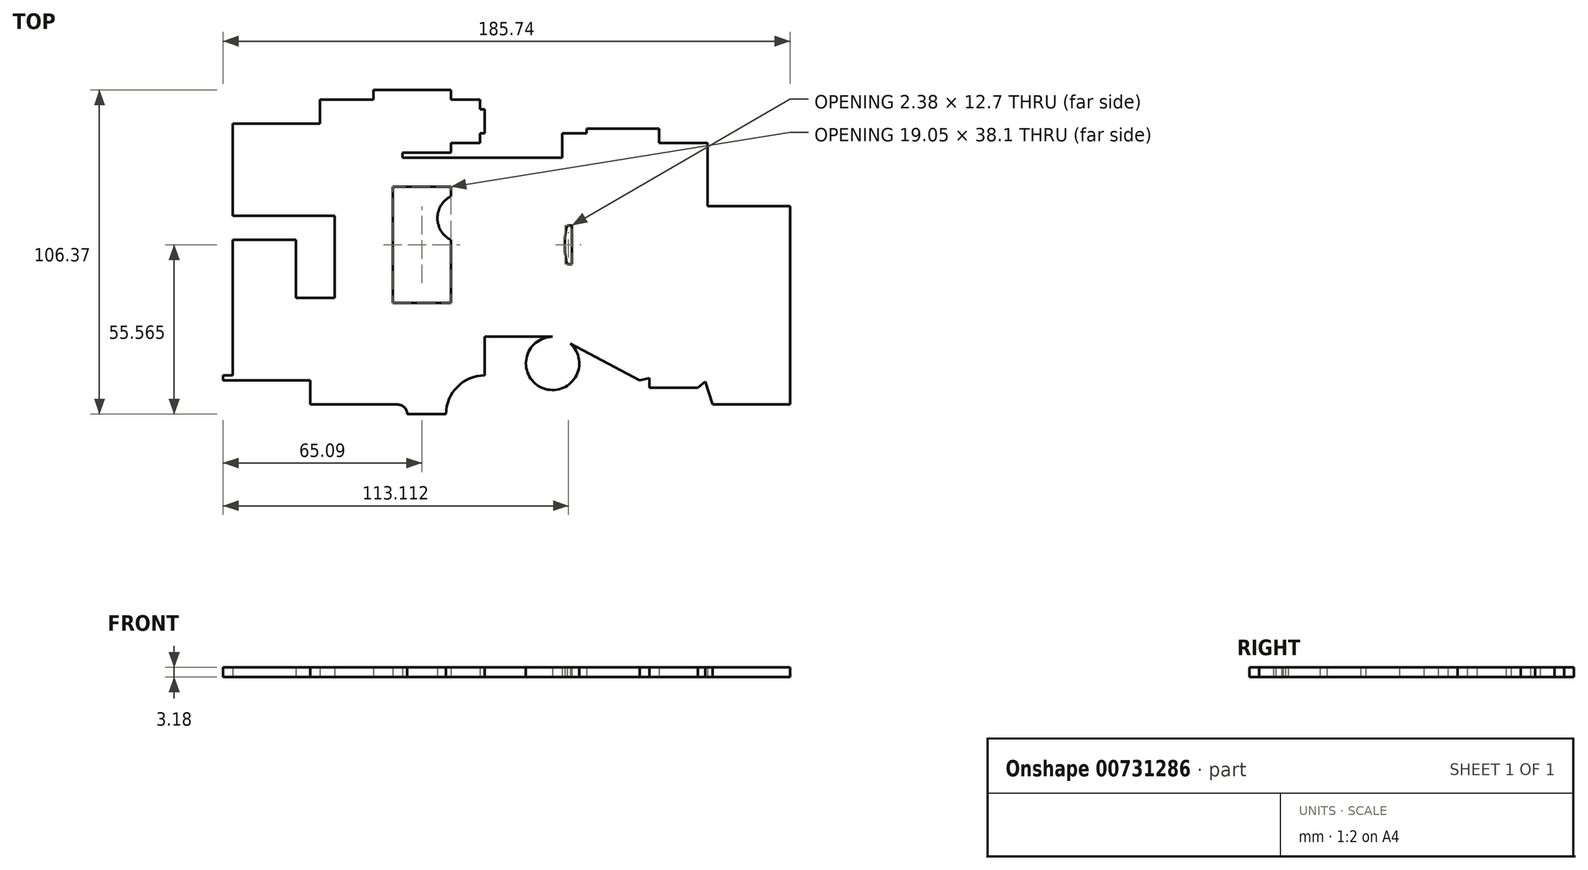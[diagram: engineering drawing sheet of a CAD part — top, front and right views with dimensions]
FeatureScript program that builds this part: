
annotation { "Feature Type Name" : "Feature", "Feature Type Description" : "" }
export const myFeature = defineFeature(function(context is Context, id is Id, definition is map)
    precondition{}
    {
        {
            var Q0;
            Q0=qCreatedBy(makeId("Top.planeOp"),FACE);
            var sketch = newSketch(context, id + "F0", { "sketchPlane" : qUnion([Q0])});
            skLineSegment(sketch, "E0.bottom", {"start": v(-55.56, 35.73) * mm, "end": v(-34.92, 35.73) * mm});
            skLineSegment(sketch, "E0.left", {"start": v(-55.56, 35.73) * mm, "end": v(-55.56, -8.72) * mm});
            skLineSegment(sketch, "E1", {"start": v(-55.56, -8.72) * mm, "end": v(-58.74, -8.72) * mm});
            skLineSegment(sketch, "E2", {"start": v(-58.74, -8.72) * mm, "end": v(-58.74, -10.3) * mm});
            skLineSegment(sketch, "E3", {"start": v(-58.74, -10.3) * mm, "end": v(-30.16, -10.3) * mm});
            skLineSegment(sketch, "E4", {"start": v(-30.16, -10.3) * mm, "end": v(-30.16, -18.24) * mm});
            skLineSegment(sketch, "E5", {"start": v(-30.16, -18.24) * mm, "end": v(-1.59, -18.24) * mm});
            skLineSegment(sketch, "E6", {"start": v(1.59, -21.42) * mm, "end": v(14.29, -21.42) * mm});
            skLineSegment(sketch, "E7", {"start": v(26.99, -8.72) * mm, "end": v(26.99, 3.98) * mm});
            skLineSegment(sketch, "E8", {"start": v(-34.92, 35.73) * mm, "end": v(-34.93, 16.68) * mm});
            skLineSegment(sketch, "E9", {"start": v(-34.92, 16.68) * mm, "end": v(-22.22, 16.68) * mm});
            skLineSegment(sketch, "E10", {"start": v(-22.22, 16.68) * mm, "end": v(-22.22, 43.67) * mm});
            skLineSegment(sketch, "E11", {"start": v(-22.22, 43.67) * mm, "end": v(-55.56, 43.67) * mm});
            skLineSegment(sketch, "E12", {"start": v(-55.56, 43.67) * mm, "end": v(-55.56, 73.83) * mm});
            skLineSegment(sketch, "E13", {"start": v(-55.56, 73.83) * mm, "end": v(-26.99, 73.83) * mm});
            skLineSegment(sketch, "E14", {"start": v(-26.99, 73.83) * mm, "end": v(-26.99, 81.77) * mm});
            skLineSegment(sketch, "E15", {"start": v(-26.99, 81.77) * mm, "end": v(-9.53, 81.77) * mm});
            skLineSegment(sketch, "E16", {"start": v(-9.53, 81.77) * mm, "end": v(-9.53, 84.95) * mm});
            skLineSegment(sketch, "E17", {"start": v(-9.53, 84.95) * mm, "end": v(15.87, 84.95) * mm});
            skLineSegment(sketch, "E18", {"start": v(15.87, 84.95) * mm, "end": v(15.87, 81.77) * mm});
            skLineSegment(sketch, "E19", {"start": v(15.87, 81.77) * mm, "end": v(25.4, 81.77) * mm});
            skLineSegment(sketch, "E20", {"start": v(25.4, 81.77) * mm, "end": v(25.4, 78.6) * mm});
            skLineSegment(sketch, "E21", {"start": v(25.4, 78.6) * mm, "end": v(26.99, 78.6) * mm});
            skLineSegment(sketch, "E22", {"start": v(26.99, 78.6) * mm, "end": v(26.99, 70.66) * mm});
            skLineSegment(sketch, "E23", {"start": v(26.99, 70.66) * mm, "end": v(25.4, 70.66) * mm});
            skLineSegment(sketch, "E24", {"start": v(25.4, 70.66) * mm, "end": v(25.4, 67.48) * mm});
            skLineSegment(sketch, "E25", {"start": v(25.4, 67.48) * mm, "end": v(15.87, 67.48) * mm});
            skLineSegment(sketch, "E26", {"start": v(15.87, 67.48) * mm, "end": v(15.87, 64.3) * mm});
            skLineSegment(sketch, "E27", {"start": v(15.87, 64.3) * mm, "end": v(0, 64.3) * mm});
            skLineSegment(sketch, "E28", {"start": v(0, 64.3) * mm, "end": v(0, 62.72) * mm});
            skLineSegment(sketch, "E29", {"start": v(0, 62.72) * mm, "end": v(52.39, 62.72) * mm});
            skLineSegment(sketch, "E30", {"start": v(52.39, 62.72) * mm, "end": v(52.39, 70.66) * mm});
            skLineSegment(sketch, "E31", {"start": v(52.39, 70.66) * mm, "end": v(60.33, 70.66) * mm});
            skLineSegment(sketch, "E32", {"start": v(60.33, 70.66) * mm, "end": v(60.33, 72.25) * mm});
            skLineSegment(sketch, "E33", {"start": v(60.33, 72.25) * mm, "end": v(66.67, 72.25) * mm});
            skLineSegment(sketch, "E34", {"start": v(66.67, 72.25) * mm, "end": v(84.14, 72.25) * mm});
            skLineSegment(sketch, "E35", {"start": v(84.14, 72.25) * mm, "end": v(84.14, 67.48) * mm});
            skLineSegment(sketch, "E36", {"start": v(84.14, 67.48) * mm, "end": v(100.01, 67.48) * mm});
            skLineSegment(sketch, "E37", {"start": v(100.01, 67.48) * mm, "end": v(100.01, 46.85) * mm});
            skLineSegment(sketch, "E38", {"start": v(100.01, 46.85) * mm, "end": v(127, 46.85) * mm});
            skLineSegment(sketch, "E39", {"start": v(127, 46.85) * mm, "end": v(127, -18.24) * mm});
            skLineSegment(sketch, "E40", {"start": v(127, -18.24) * mm, "end": v(119.06, -18.24) * mm});
            skLineSegment(sketch, "E41", {"start": v(119.06, -18.24) * mm, "end": v(104.78, -18.24) * mm});
            skLineSegment(sketch, "E42", {"start": v(104.78, -18.24) * mm, "end": v(101.6, -18.24) * mm});
            skLineSegment(sketch, "E43", {"start": v(99.16, -10.69) * mm, "end": v(101.6, -18.24) * mm});
            skLineSegment(sketch, "E44", {"start": v(80.88, -9.58) * mm, "end": v(77.79, -10.3) * mm});
            skLineSegment(sketch, "E45", {"start": v(80.88, -9.58) * mm, "end": v(80.88, -12.75) * mm});
            skLineSegment(sketch, "E46", {"start": v(80.88, -12.75) * mm, "end": v(96.75, -12.75) * mm});
            skLineSegment(sketch, "E47", {"start": v(96.75, -12.75) * mm, "end": v(99.16, -10.69) * mm});
            skPoint(sketch, "E48", {"position": v(99.16, -10.69) * mm});
            skArc(sketch, "E49", {"start": v(26.99, -8.72) * mm, "mid": v(18, -12.44) * mm, "end": v(14.29, -21.42) * mm});
            skArc(sketch, "E50", {"start": v(-1.59, -18.24) * mm, "mid": v(0.66, -19.17) * mm, "end": v(1.59, -21.42) * mm});
            skLineSegment(sketch, "E51", {"start": v(49.21, 3.98) * mm, "end": v(49.21, -13.48) * mm});
            skCircle(sketch, "E52", {"center": v(49.21, -4.75) * mm, "radius": 8.73 * mm});
            skLineSegment(sketch, "E53", {"start": v(49.21, 3.98) * mm, "end": v(26.99, 3.98) * mm});
            skPoint(sketch, "E54", {"position": v(55.05, 1.73) * mm});
            skLineSegment(sketch, "E55", {"start": v(55.05, 1.73) * mm, "end": v(77.79, -10.3) * mm});
            skLineSegment(sketch, "E56", {"start": v(15.88, 53.2) * mm, "end": v(15.88, 50.02) * mm});
            skLineSegment(sketch, "E57", {"start": v(15.88, 50.02) * mm, "end": v(15.88, 35.73) * mm});
            skLineSegment(sketch, "E58", {"start": v(15.88, 53.2) * mm, "end": v(15.88, 15.1) * mm});
            skLineSegment(sketch, "E59", {"start": v(15.88, 15.1) * mm, "end": v(15.88, 18.27) * mm});
            skLineSegment(sketch, "E60", {"start": v(15.88, 18.27) * mm, "end": v(15.88, 32.56) * mm});
            skLineSegment(sketch, "E61", {"start": v(15.88, 32.56) * mm, "end": v(15.88, 18.27) * mm});
            skLineSegment(sketch, "E62", {"start": v(15.88, 15.1) * mm, "end": v(-3.17, 15.1) * mm});
            skLineSegment(sketch, "E63", {"start": v(-3.17, 15.1) * mm, "end": v(-3.17, 53.2) * mm});
            skLineSegment(sketch, "E64", {"start": v(-3.17, 53.2) * mm, "end": v(15.88, 53.2) * mm});
            skLineSegment(sketch, "E65", {"start": v(39.69, 53.2) * mm, "end": v(15.88, 53.2) * mm});
            skLineSegment(sketch, "E66", {"start": v(55.56, 15.1) * mm, "end": v(55.56, 53.2) * mm});
            skLineSegment(sketch, "E67", {"start": v(55.56, 53.2) * mm, "end": v(39.69, 53.2) * mm});
            skLineSegment(sketch, "E68", {"start": v(55.56, 53.2) * mm, "end": v(55.56, 40.5) * mm});
            skLineSegment(sketch, "E69", {"start": v(55.56, 15.1) * mm, "end": v(55.56, 27.8) * mm});
            skLineSegment(sketch, "E70", {"start": v(55.56, 27.8) * mm, "end": v(53.98, 27.8) * mm});
            skLineSegment(sketch, "E71", {"start": v(55.56, 40.5) * mm, "end": v(53.98, 40.5) * mm});
            skArc(sketch, "E72", {"start": v(53.98, 40.5) * mm, "mid": v(53.18, 34.15) * mm, "end": v(53.98, 27.8) * mm});
            skArc(sketch, "E73", {"start": v(15.88, 50.02) * mm, "mid": v(11.48, 42.88) * mm, "end": v(15.88, 35.73) * mm});
            skArc(sketch, "E74", {"start": v(15.88, 32.56) * mm, "mid": v(11.48, 25.41) * mm, "end": v(15.88, 18.27) * mm});
            skLineSegment(sketch, "E75", {"start": v(39.69, 53.2) * mm, "end": v(39.69, 50.02) * mm});
            skPoint(sketch, "E76", {"position": v(47.63, 15.1) * mm});
            skLineSegment(sketch, "E77", {"start": v(47.63, 18.27) * mm, "end": v(39.69, 15.1) * mm});
            skLineSegment(sketch, "E78", {"start": v(55.56, 15.1) * mm, "end": v(47.63, 18.27) * mm});
            skLineSegment(sketch, "E79", {"start": v(39.69, 15.1) * mm, "end": v(39.69, 18.27) * mm});
            skLineSegment(sketch, "E80", {"start": v(39.69, 50.02) * mm, "end": v(39.69, 35.73) * mm});
            skLineSegment(sketch, "E81", {"start": v(39.69, 18.27) * mm, "end": v(39.69, 32.56) * mm});
            skLineSegment(sketch, "E82", {"start": v(39.69, 32.56) * mm, "end": v(39.69, 35.73) * mm});
            skArc(sketch, "E83", {"start": v(39.69, 35.73) * mm, "mid": v(44.09, 42.88) * mm, "end": v(39.69, 50.02) * mm});
            skArc(sketch, "E84", {"start": v(39.69, 18.27) * mm, "mid": v(44.09, 25.41) * mm, "end": v(39.69, 32.56) * mm});
            skSolve(sketch);
        }
        {
            var Q0;
            Q0=makeQuery(id+"F0.imprint","IMPRINT",FACE,{"disambiguationData":[TD([[makeQuery(id+"F0.imprint","IMPRINT",EDGE,{"derivedFrom":sQuery(id+"F0.wireOp",EDGE,"E0.bottom")}),-1.0]])]});
            var Q1;
            Q1=makeQuery(id+"F0.imprint","IMPRINT",FACE,{"disambiguationData":[TD([[makeQuery(id+"F0.imprint","IMPRINT",EDGE,{"derivedFrom":sQuery(id+"F0.wireOp",EDGE,"E57")}),-1.0]])]});
            var Q2;
            Q2=makeQuery(id+"F0.imprint","IMPRINT",FACE,{"disambiguationData":[TD([[makeQuery(id+"F0.imprint","IMPRINT",EDGE,{"derivedFrom":sQuery(id+"F0.wireOp",EDGE,"E61")}),-1.0]])]});
            var Q3;
            Q3=makeQuery(id+"F0.imprint","IMPRINT",FACE,{"disambiguationData":[TD([[makeQuery(id+"F0.imprint","IMPRINT",EDGE,{"derivedFrom":sQuery(id+"F0.wireOp",EDGE,"E80")}),1.0]])]});
            var Q4;
            Q4=makeQuery(id+"F0.imprint","IMPRINT",FACE,{"disambiguationData":[TD([[makeQuery(id+"F0.imprint","IMPRINT",EDGE,{"derivedFrom":sQuery(id+"F0.wireOp",EDGE,"E81")}),-1.0]])]});
            var Q5;
            Q5=makeQuery(id+"F0.imprint","IMPRINT",FACE,{"disambiguationData":[TD([[makeQuery(id+"F0.imprint","IMPRINT",EDGE,{"derivedFrom":sQuery(id+"F0.wireOp",EDGE,"E66")}),1.0]])]});
            var Q6;
            {var subQ0=sQuery(id+"F0.wireOp",EDGE,"E51");Q6=makeQuery(id+"F0.imprint","IMPRINT",FACE,{"disambiguationData":[TD([[makeQuery(id+"F0.imprint","IMPRINT",EDGE,{"derivedFrom":subQ0}),1.0]])]});}
            var Q7;
            {var subQ0=sQuery(id+"F0.wireOp",EDGE,"E51");Q7=makeQuery(id+"F0.imprint","IMPRINT",FACE,{"disambiguationData":[TD([[makeQuery(id+"F0.imprint","IMPRINT",EDGE,{"derivedFrom":subQ0}),-1.0]])]});}
            extrude(context, id + "F1", {"entities" : qUnion([Q0, Q1, Q2, Q3, Q4, Q5, Q6, Q7]), "depth" : 3.17 * mm, "offsetDistance" : 25.4 * mm});
        }
    });
